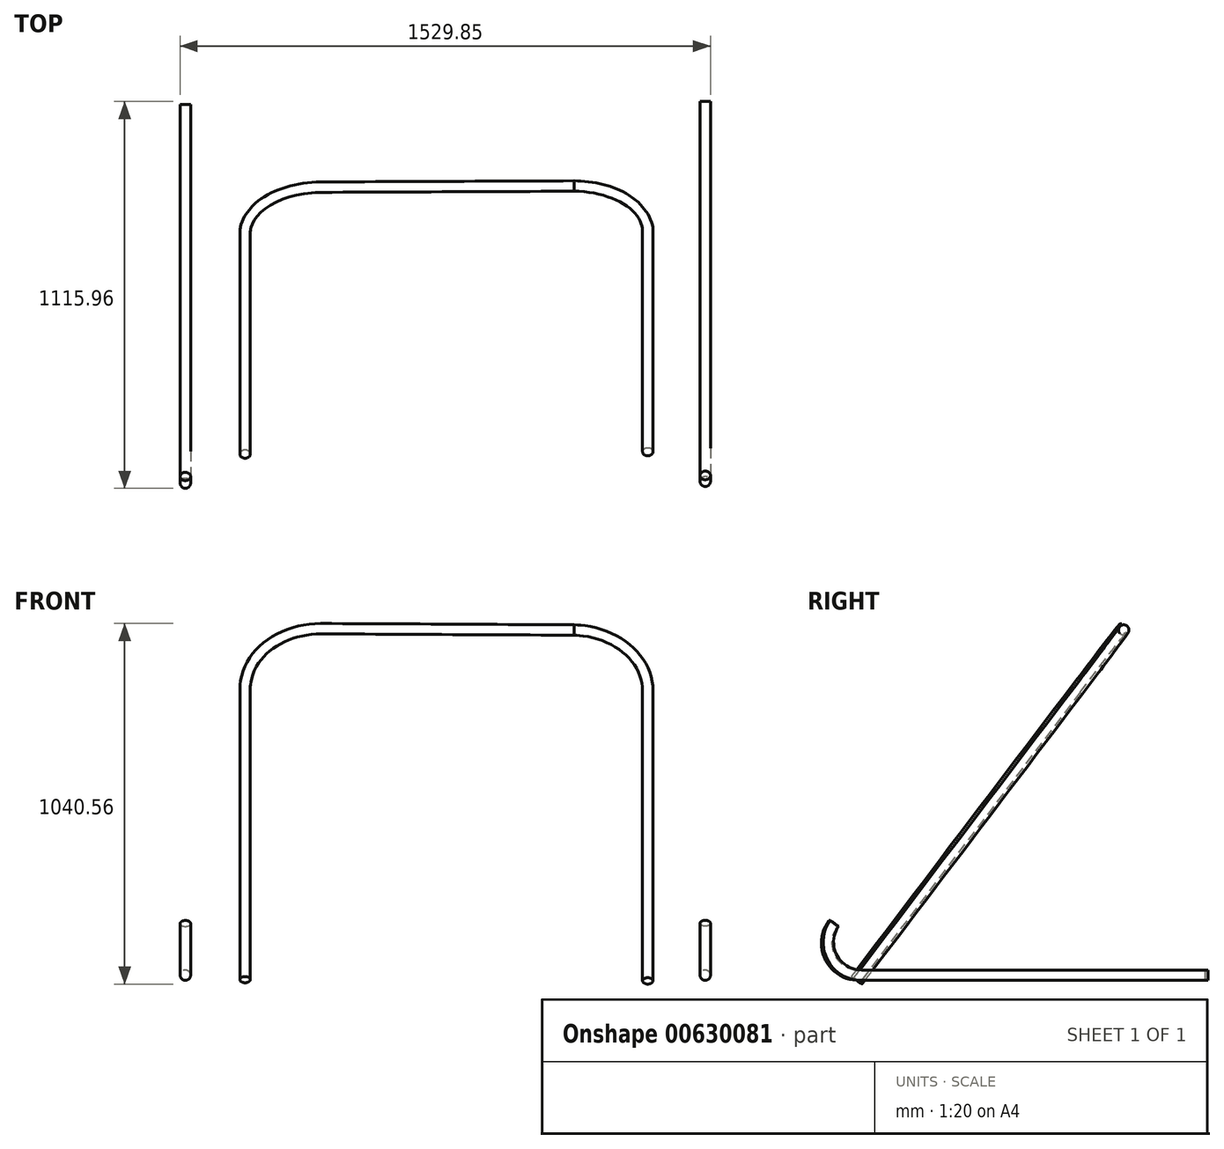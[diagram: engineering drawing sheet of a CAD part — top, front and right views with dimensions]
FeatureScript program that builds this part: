
annotation { "Feature Type Name" : "Feature", "Feature Type Description" : "" }
export const myFeature = defineFeature(function(context is Context, id is Id, definition is map)
    precondition{}
    {
        {
            var Q0;
            Q0=qCreatedBy(makeId("Front.planeOp"),FACE);
            var sketch = newSketch(context, id + "F0", { "sketchPlane" : qUnion([Q0])});
            skLineSegment(sketch, "E0", {"start": v(0, 1000) * mm, "end": v(500, 1000) * mm});
            skLineSegment(sketch, "E1", {"start": v(0, 1000) * mm, "end": v(-500, 1000) * mm});
            skSolve(sketch);
        }
        {
            var Q0;
            Q0=sQuery(id+"F0.wireOp",VERTEX,"E0.end");
            var Q1;
            Q1=qCreatedBy(makeId("Right.planeOp"),FACE);
            cPlane(context, id + "F1", {"entities" : qUnion([Q0, Q1]), "cplaneType" : CPlaneType.PLANE_POINT, "offset" : 25 * mm, "width" : 150 * mm, "height" : 150 * mm});
        }
        {
            var Q0;
            Q0=qCreatedBy(id+"F1.planeOp",FACE);
            var sketch = newSketch(context, id + "F2", { "sketchPlane" : qUnion([Q0])});
            skLineSegment(sketch, "E2", {"start": v(245.22, 0) * mm, "end": v(-754.78, 0) * mm});
            skArc(sketch, "E3", {"start": v(-754.78, 0) * mm, "mid": v(-839.5, 51.17) * mm, "end": v(-833.62, 149.96) * mm});
            skSolve(sketch);
        }
        {
            var Q0;
            Q0=qCreatedBy(makeId("Front.planeOp"),FACE);
            var sketch = newSketch(context, id + "F3", { "sketchPlane" : qUnion([Q0])});
            skCircle(sketch, "E4", {"center": v(750.03, 0) * mm, "radius": 15 * mm});
            skSolve(sketch);
        }
        {
            var Q0;
            Q0=sQuery(id+"F0.wireOp",VERTEX,"E1.end");
            var Q1;
            Q1=qCreatedBy(makeId("Right.planeOp"),FACE);
            cPlane(context, id + "F4", {"entities" : qUnion([Q0, Q1]), "cplaneType" : CPlaneType.PLANE_POINT, "offset" : 25 * mm, "width" : 150 * mm, "height" : 150 * mm});
        }
        {
            var Q0;
            Q0=qCreatedBy(id+"F4.planeOp",FACE);
            var sketch = newSketch(context, id + "F5", { "sketchPlane" : qUnion([Q0])});
            skLineSegment(sketch, "E5", {"start": v(236.77, 0) * mm, "end": v(-763.23, 0) * mm});
            skArc(sketch, "E6", {"start": v(-763.23, 0) * mm, "mid": v(-846.23, 51.64) * mm, "end": v(-836.56, 148.91) * mm});
            skSolve(sketch);
        }
        {
            var Q0;
            Q0=qCreatedBy(makeId("Front.planeOp"),FACE);
            var sketch = newSketch(context, id + "F6", { "sketchPlane" : qUnion([Q0])});
            skCircle(sketch, "E7", {"center": v(-749.82, 0) * mm, "radius": 15 * mm});
            skSolve(sketch);
        }
        {
            var Q0;
            Q0=sQuery(id+"F5.wireOp",VERTEX,"E6.end");
            var Q1;
            Q1=sQuery(id+"F2.wireOp",VERTEX,"E3.end");
            var Q2;
            Q2=sQuery(id+"F0.wireOp",VERTEX,"E1.start");
            cPlane(context, id + "F7", {"entities" : qUnion([Q0, Q1, Q2]), "cplaneType" : CPlaneType.THREE_POINT, "offset" : 25 * mm, "width" : 150 * mm, "height" : 150 * mm});
        }
        {
            var Q0;
            Q0=qCreatedBy(id+"F7.planeOp",FACE);
            var sketch = newSketch(context, id + "F8", { "sketchPlane" : qUnion([Q0])});
            skLineSegment(sketch, "E8", {"start": v(500.6, -476.86) * mm, "end": v(500.6, 576.08) * mm});
            skArc(sketch, "E9", {"start": v(500.6, 576.08) * mm, "mid": v(460.36, 673.72) * mm, "end": v(363.02, 714.67) * mm});
            skLineSegment(sketch, "E10", {"start": v(-499.05, -475.64) * mm, "end": v(-499.05, 576.08) * mm});
            skArc(sketch, "E11", {"start": v(-499.05, 576.08) * mm, "mid": v(-460.35, 671.7) * mm, "end": v(-366.03, 713.5) * mm});
            skLineSegment(sketch, "E12", {"start": v(363.02, 714.67) * mm, "end": v(-366.03, 713.5) * mm});
            skSolve(sketch);
        }
        {
            var Q0;
            Q0 = qSketchRegion(id + "F3", true);
            var Q1;
            Q1 = qConstructionFilter(qBodyType(qCreatedBy(id + "F2" ,EDGE), BodyType.WIRE), ConstructionObject.NO);
            sweep(context, id + "F9", {"profiles" : qUnion([Q0]), "path" : qUnion([Q1])});
        }
        {
            var Q0;
            Q0 = qSketchRegion(id + "F6", true);
            var Q1;
            Q1 = qConstructionFilter(qBodyType(qCreatedBy(id + "F5" ,EDGE), BodyType.WIRE), ConstructionObject.NO);
            sweep(context, id + "F10", {"profiles" : qUnion([Q0]), "path" : qUnion([Q1])});
        }
        {
            var Q0;
            Q0=qCreatedBy(makeId("Right.planeOp"),FACE);
            var sketch = newSketch(context, id + "F11", { "sketchPlane" : qUnion([Q0])});
            skCircle(sketch, "E13", {"center": v(0, 998.2) * mm, "radius": 15 * mm});
            skSolve(sketch);
        }
        {
            var Q0;
            Q0 = qSketchRegion(id + "F11", true);
            var Q1;
            Q1 = qConstructionFilter(qBodyType(qCreatedBy(id + "F8" ,EDGE), BodyType.WIRE), ConstructionObject.NO);
            sweep(context, id + "F12", {"profiles" : qUnion([Q0]), "path" : qUnion([Q1])});
        }
    });
